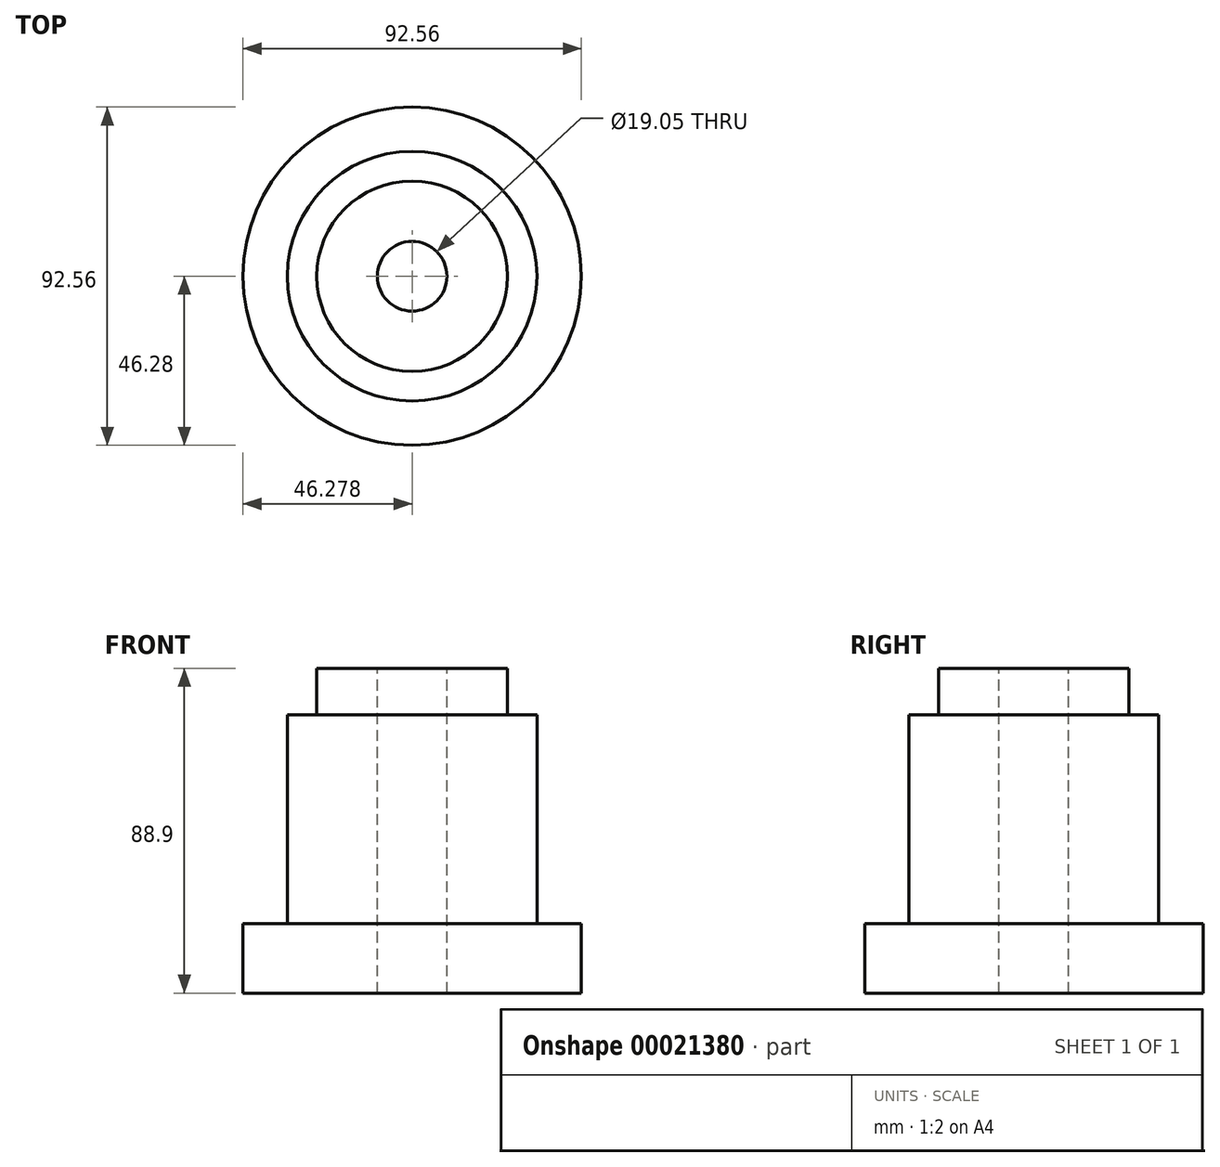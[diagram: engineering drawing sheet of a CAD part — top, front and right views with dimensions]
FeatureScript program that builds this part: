
annotation { "Feature Type Name" : "Feature", "Feature Type Description" : "" }
export const myFeature = defineFeature(function(context is Context, id is Id, definition is map)
    precondition{}
    {
        {
            var Q0;
            Q0=qCreatedBy(makeId("Front.planeOp"),FACE);
            var sketch = newSketch(context, id + "F0", { "sketchPlane" : qUnion([Q0])});
            skLineSegment(sketch, "E0.bottom", {"start": v(-27.64, 42.03) * mm, "end": v(-11.09, 42.03) * mm});
            skLineSegment(sketch, "E0.top", {"start": v(-27.64, 29.33) * mm, "end": v(-11.09, 29.33) * mm});
            skLineSegment(sketch, "E0.right", {"start": v(-11.09, 42.03) * mm, "end": v(-11.09, 29.33) * mm});
            skLineSegment(sketch, "E1.bottom", {"start": v(-27.64, 29.33) * mm, "end": v(-3, 29.33) * mm});
            skLineSegment(sketch, "E1.top", {"start": v(-27.64, -27.82) * mm, "end": v(-3, -27.82) * mm});
            skLineSegment(sketch, "E1.right", {"start": v(-3, 29.33) * mm, "end": v(-3, -27.82) * mm});
            skLineSegment(sketch, "E2.bottom", {"start": v(-27.64, -27.82) * mm, "end": v(9.12, -27.82) * mm});
            skLineSegment(sketch, "E2.top", {"start": v(-27.64, -46.87) * mm, "end": v(9.12, -46.87) * mm});
            skLineSegment(sketch, "E2.right", {"start": v(9.12, -27.82) * mm, "end": v(9.12, -46.87) * mm});
            skPoint(sketch, "E3.trimOffspring.end.orphan", {"position": v(-11.18, -46.87) * mm});
            skLineSegment(sketch, "E4", {"start": v(-27.64, 42.03) * mm, "end": v(-27.64, -46.87) * mm});
            skPoint(sketch, "E5.end.orphan", {"position": v(-37.16, -46.87) * mm});
            skPoint(sketch, "E5.start.orphan", {"position": v(-37.16, 42.03) * mm});
            skLineSegment(sketch, "E6", {"start": v(-37.16, 42.03) * mm, "end": v(-37.16, -46.87) * mm});
            skSolve(sketch);
        }
        {
            var Q0;
            Q0 = qSketchRegion(id + "F0", true);
            var Q1;
            Q1=sQuery(id+"F0.wireOp",EDGE,"E6");
            revolve(context, id + "F1", {"entities" : qUnion([Q0]), "axis" : qUnion([Q1]), "revolveType" : RevolveType.FULL});
        }
    });
